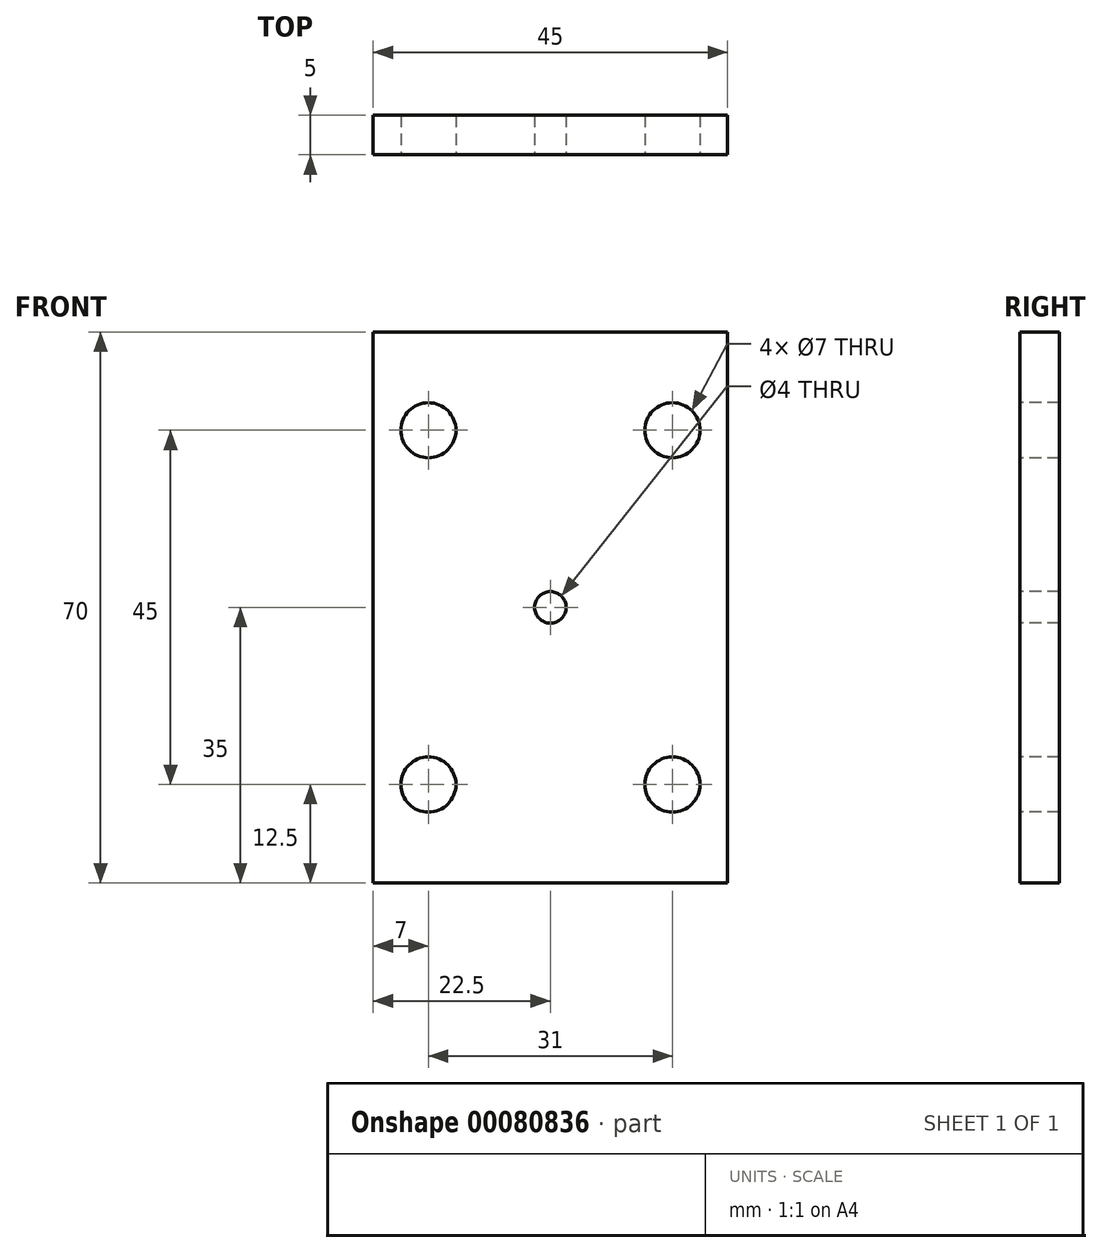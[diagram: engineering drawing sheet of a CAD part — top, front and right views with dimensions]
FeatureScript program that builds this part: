
annotation { "Feature Type Name" : "Feature", "Feature Type Description" : "" }
export const myFeature = defineFeature(function(context is Context, id is Id, definition is map)
    precondition{}
    {
        {
            var Q0;
            Q0=qCreatedBy(makeId("Front.planeOp"),FACE);
            var sketch = newSketch(context, id + "F0", { "sketchPlane" : qUnion([Q0])});
            skLineSegment(sketch, "E0.bottom", {"start": v(22.5, -35) * mm, "end": v(-22.5, -35) * mm});
            skLineSegment(sketch, "E0.top", {"start": v(22.5, 35) * mm, "end": v(-22.5, 35) * mm});
            skLineSegment(sketch, "E0.left", {"start": v(22.5, -35) * mm, "end": v(22.5, 35) * mm});
            skLineSegment(sketch, "E0.right", {"start": v(-22.5, -35) * mm, "end": v(-22.5, 35) * mm});
            skPoint(sketch, "E0.middle", {"position": v(0, 0) * mm});
            skSolve(sketch);
        }
        {
            var Q0;
            Q0=makeQuery(id+"F0.imprint","IMPRINT",FACE,{"disambiguationData":[TD([[makeQuery(id+"F0.imprint","IMPRINT",EDGE,{"derivedFrom":sQuery(id+"F0.wireOp",EDGE,"E0.bottom")}),-1.0]])]});
            extrude(context, id + "F1", {"entities" : qUnion([Q0]), "depth" : 5 * mm});
        }
        {
            var Q0;
            Q0=makeQuery(id+"F1.opExtrude","CAP_FACE",FACE,{"disambiguationData":[OSD([sQuery(id+"F0.wireOp",EDGE,"E0.bottom"),sQuery(id+"F0.wireOp",EDGE,"E0.top"),sQuery(id+"F0.wireOp",EDGE,"E0.left"),sQuery(id+"F0.wireOp",EDGE,"E0.right")])],"isStart":false});
            var sketch = newSketch(context, id + "F2", { "sketchPlane" : qUnion([Q0])});
            skLineSegment(sketch, "E1.bottom", {"start": v(15.5, -22.5) * mm, "end": v(-15.5, -22.5) * mm, "construction": true});
            skLineSegment(sketch, "E1.top", {"start": v(15.5, 22.5) * mm, "end": v(-15.5, 22.5) * mm, "construction": true});
            skLineSegment(sketch, "E1.left", {"start": v(15.5, -22.5) * mm, "end": v(15.5, 22.5) * mm, "construction": true});
            skLineSegment(sketch, "E1.right", {"start": v(-15.5, -22.5) * mm, "end": v(-15.5, 22.5) * mm, "construction": true});
            skPoint(sketch, "E1.middle", {"position": v(0, 0) * mm});
            skCircle(sketch, "E2", {"center": v(-15.5, 22.5) * mm, "radius": 3.5 * mm});
            skCircle(sketch, "E3", {"center": v(15.5, 22.5) * mm, "radius": 3.5 * mm});
            skCircle(sketch, "E4", {"center": v(-15.5, -22.5) * mm, "radius": 3.5 * mm});
            skCircle(sketch, "E5", {"center": v(15.5, -22.5) * mm, "radius": 3.5 * mm});
            skCircle(sketch, "E6", {"center": v(0, 0) * mm, "radius": 2 * mm});
            skSolve(sketch);
        }
        {
            var Q0;
            Q0=makeQuery(id+"F2.imprint","IMPRINT",FACE,{"disambiguationData":[TD([[makeQuery(id+"F2.imprint","IMPRINT",EDGE,{"derivedFrom":sQuery(id+"F2.wireOp",EDGE,"E2")}),1.0]])]});
            var Q1;
            Q1=makeQuery(id+"F2.imprint","IMPRINT",FACE,{"disambiguationData":[TD([[makeQuery(id+"F2.imprint","IMPRINT",EDGE,{"derivedFrom":sQuery(id+"F2.wireOp",EDGE,"E3")}),1.0]])]});
            var Q2;
            Q2=makeQuery(id+"F2.imprint","IMPRINT",FACE,{"disambiguationData":[TD([[makeQuery(id+"F2.imprint","IMPRINT",EDGE,{"derivedFrom":sQuery(id+"F2.wireOp",EDGE,"E4")}),1.0]])]});
            var Q3;
            Q3=makeQuery(id+"F2.imprint","IMPRINT",FACE,{"disambiguationData":[TD([[makeQuery(id+"F2.imprint","IMPRINT",EDGE,{"derivedFrom":sQuery(id+"F2.wireOp",EDGE,"E5")}),1.0]])]});
            var Q4;
            Q4=makeQuery(id+"F2.imprint","IMPRINT",FACE,{"disambiguationData":[TD([[makeQuery(id+"F2.imprint","IMPRINT",EDGE,{"derivedFrom":sQuery(id+"F2.wireOp",EDGE,"E6")}),1.0]])]});
            extrude(context, id + "F3", {"entities" : qUnion([Q0, Q1, Q2, Q3, Q4]), "operationType" : NewBodyOperationType.REMOVE, "endBound" : BoundingType.UP_TO_NEXT, "oppositeDirection" : true, "depth" : 25 * mm});
        }
    });
